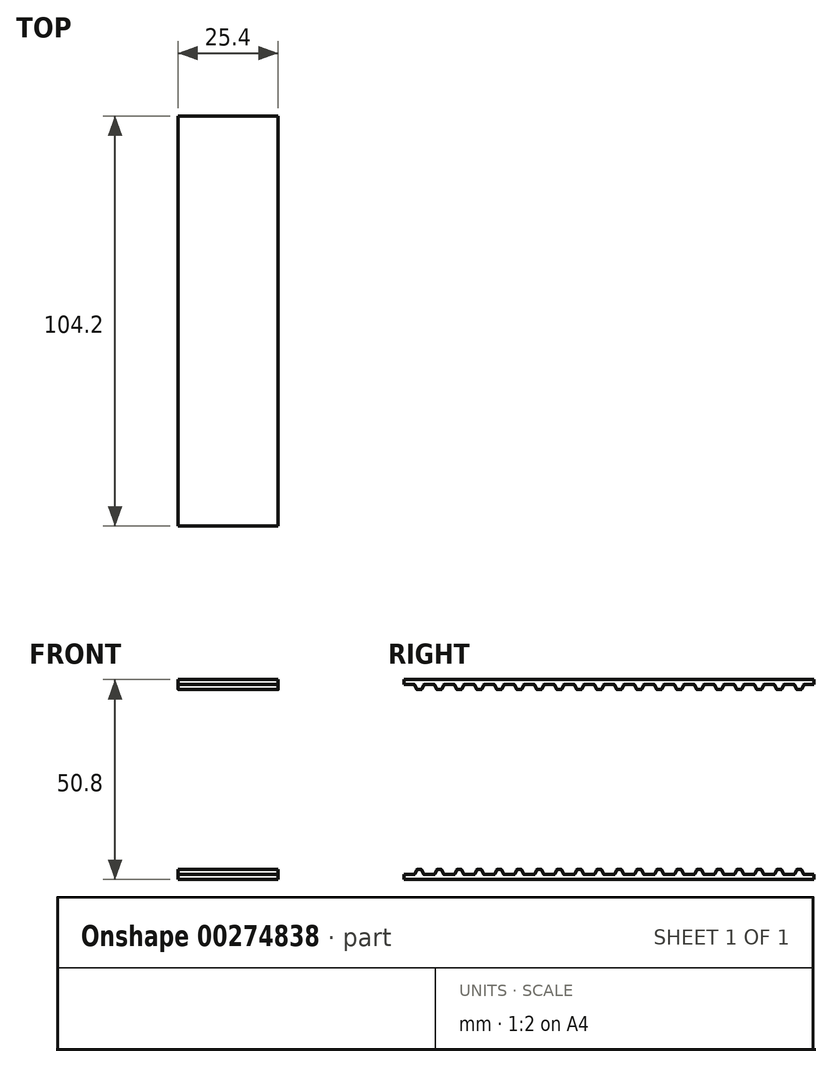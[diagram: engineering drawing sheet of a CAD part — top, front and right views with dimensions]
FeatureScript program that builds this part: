
annotation { "Feature Type Name" : "Feature", "Feature Type Description" : "" }
export const myFeature = defineFeature(function(context is Context, id is Id, definition is map)
    precondition{}
    {
        {
            var Q0;
            Q0=qCreatedBy(makeId("Right.planeOp"),FACE);
            var sketch = newSketch(context, id + "F0", { "sketchPlane" : qUnion([Q0])});
            skLineSegment(sketch, "E0", {"start": v(-151.26, 0) * mm, "end": v(153.54, 0) * mm, "construction": true});
            skLineSegment(sketch, "E1", {"start": v(-25.4, 25.4) * mm, "end": v(78.8, 25.4) * mm});
            skLineSegment(sketch, "E2", {"start": v(-25.4, 24.13) * mm, "end": v(-22.86, 24.13) * mm});
            skLineSegment(sketch, "E3", {"start": v(-22.62, 23.96) * mm, "end": v(-22.28, 23.03) * mm});
            skLineSegment(sketch, "E4", {"start": v(-22.04, 22.86) * mm, "end": v(-21.08, 22.86) * mm});
            skLineSegment(sketch, "E5", {"start": v(-20.84, 23.03) * mm, "end": v(-20.5, 23.96) * mm});
            skPoint(sketch, "E6", {"position": v(-22.45, 23.5) * mm});
            skPoint(sketch, "E7", {"position": v(-20.67, 23.5) * mm});
            skLineSegment(sketch, "E8", {"start": v(-20.26, 24.13) * mm, "end": v(-17.78, 24.13) * mm});
            skPoint(sketch, "E9.visualSharp", {"position": v(-22.68, 24.13) * mm});
            skArc(sketch, "E9.filletArc", {"start": v(-22.62, 23.96) * mm, "mid": v(-22.71, 24.08) * mm, "end": v(-22.86, 24.13) * mm});
            skPoint(sketch, "E10.visualSharp", {"position": v(-22.22, 22.86) * mm});
            skArc(sketch, "E10.filletArc", {"start": v(-22.28, 23.03) * mm, "mid": v(-22.19, 22.9) * mm, "end": v(-22.04, 22.86) * mm});
            skPoint(sketch, "E11.visualSharp", {"position": v(-20.9, 22.86) * mm});
            skArc(sketch, "E11.filletArc", {"start": v(-21.08, 22.86) * mm, "mid": v(-20.94, 22.9) * mm, "end": v(-20.84, 23.03) * mm});
            skPoint(sketch, "E12.visualSharp", {"position": v(-20.44, 24.13) * mm});
            skArc(sketch, "E12.filletArc", {"start": v(-20.26, 24.13) * mm, "mid": v(-20.4, 24.08) * mm, "end": v(-20.5, 23.96) * mm});
            skPoint(sketch, "E13.1.0.0", {"position": v(-15.82, 22.86) * mm});
            skLineSegment(sketch, "E13.1.0.1", {"start": v(-15.76, 23.03) * mm, "end": v(-15.42, 23.96) * mm});
            skLineSegment(sketch, "E13.1.0.2", {"start": v(-16.96, 22.86) * mm, "end": v(-16, 22.86) * mm});
            skLineSegment(sketch, "E13.1.0.3", {"start": v(-17.54, 23.96) * mm, "end": v(-17.2, 23.03) * mm});
            skPoint(sketch, "E13.1.0.4", {"position": v(-17.14, 22.86) * mm});
            skPoint(sketch, "E13.1.0.5", {"position": v(-15.36, 24.13) * mm});
            skPoint(sketch, "E13.1.0.6", {"position": v(-17.37, 23.5) * mm});
            skPoint(sketch, "E13.1.0.7", {"position": v(-17.6, 24.13) * mm});
            skPoint(sketch, "E13.1.0.8", {"position": v(-15.6, 23.5) * mm});
            skArc(sketch, "E13.1.0.9", {"start": v(-17.54, 23.96) * mm, "mid": v(-17.63, 24.08) * mm, "end": v(-17.78, 24.13) * mm});
            skArc(sketch, "E13.1.0.10", {"start": v(-17.2, 23.03) * mm, "mid": v(-17.1, 22.9) * mm, "end": v(-16.96, 22.86) * mm});
            skArc(sketch, "E13.1.0.11", {"start": v(-16, 22.86) * mm, "mid": v(-15.86, 22.9) * mm, "end": v(-15.76, 23.03) * mm});
            skArc(sketch, "E13.1.0.12", {"start": v(-15.18, 24.13) * mm, "mid": v(-15.33, 24.08) * mm, "end": v(-15.42, 23.96) * mm});
            skPoint(sketch, "E13.2.0.0", {"position": v(-10.74, 22.86) * mm});
            skLineSegment(sketch, "E13.2.0.1", {"start": v(-10.68, 23.03) * mm, "end": v(-10.34, 23.96) * mm});
            skLineSegment(sketch, "E13.2.0.2", {"start": v(-11.88, 22.86) * mm, "end": v(-10.92, 22.86) * mm});
            skLineSegment(sketch, "E13.2.0.3", {"start": v(-12.46, 23.96) * mm, "end": v(-12.12, 23.03) * mm});
            skPoint(sketch, "E13.2.0.4", {"position": v(-12.06, 22.86) * mm});
            skPoint(sketch, "E13.2.0.5", {"position": v(-10.28, 24.13) * mm});
            skPoint(sketch, "E13.2.0.6", {"position": v(-12.3, 23.5) * mm});
            skPoint(sketch, "E13.2.0.7", {"position": v(-12.52, 24.13) * mm});
            skPoint(sketch, "E13.2.0.8", {"position": v(-10.51, 23.5) * mm});
            skArc(sketch, "E13.2.0.9", {"start": v(-12.46, 23.96) * mm, "mid": v(-12.55, 24.08) * mm, "end": v(-12.7, 24.13) * mm});
            skArc(sketch, "E13.2.0.10", {"start": v(-12.12, 23.03) * mm, "mid": v(-12.03, 22.9) * mm, "end": v(-11.88, 22.86) * mm});
            skArc(sketch, "E13.2.0.11", {"start": v(-10.92, 22.86) * mm, "mid": v(-10.78, 22.9) * mm, "end": v(-10.68, 23.03) * mm});
            skArc(sketch, "E13.2.0.12", {"start": v(-10.1, 24.13) * mm, "mid": v(-10.25, 24.08) * mm, "end": v(-10.34, 23.96) * mm});
            skPoint(sketch, "E13.3.0.0", {"position": v(-5.66, 22.86) * mm});
            skLineSegment(sketch, "E13.3.0.1", {"start": v(-5.6, 23.03) * mm, "end": v(-5.26, 23.96) * mm});
            skLineSegment(sketch, "E13.3.0.2", {"start": v(-6.8, 22.86) * mm, "end": v(-5.84, 22.86) * mm});
            skLineSegment(sketch, "E13.3.0.3", {"start": v(-7.38, 23.96) * mm, "end": v(-7.04, 23.03) * mm});
            skPoint(sketch, "E13.3.0.4", {"position": v(-6.98, 22.86) * mm});
            skPoint(sketch, "E13.3.0.5", {"position": v(-5.2, 24.13) * mm});
            skPoint(sketch, "E13.3.0.6", {"position": v(-7.21, 23.5) * mm});
            skPoint(sketch, "E13.3.0.7", {"position": v(-7.44, 24.13) * mm});
            skPoint(sketch, "E13.3.0.8", {"position": v(-5.43, 23.5) * mm});
            skArc(sketch, "E13.3.0.9", {"start": v(-7.38, 23.96) * mm, "mid": v(-7.47, 24.08) * mm, "end": v(-7.62, 24.13) * mm});
            skArc(sketch, "E13.3.0.10", {"start": v(-7.04, 23.03) * mm, "mid": v(-6.95, 22.9) * mm, "end": v(-6.8, 22.86) * mm});
            skArc(sketch, "E13.3.0.11", {"start": v(-5.84, 22.86) * mm, "mid": v(-5.7, 22.9) * mm, "end": v(-5.6, 23.03) * mm});
            skArc(sketch, "E13.3.0.12", {"start": v(-5.02, 24.13) * mm, "mid": v(-5.17, 24.08) * mm, "end": v(-5.26, 23.96) * mm});
            skPoint(sketch, "E13.4.0.0", {"position": v(-0.58, 22.86) * mm});
            skLineSegment(sketch, "E13.4.0.1", {"start": v(-0.52, 23.03) * mm, "end": v(-0.18, 23.96) * mm});
            skLineSegment(sketch, "E13.4.0.2", {"start": v(-1.72, 22.86) * mm, "end": v(-0.76, 22.86) * mm});
            skLineSegment(sketch, "E13.4.0.3", {"start": v(-2.3, 23.96) * mm, "end": v(-1.96, 23.03) * mm});
            skPoint(sketch, "E13.4.0.4", {"position": v(-1.9, 22.86) * mm});
            skPoint(sketch, "E13.4.0.5", {"position": v(-0.12, 24.13) * mm});
            skPoint(sketch, "E13.4.0.6", {"position": v(-2.13, 23.5) * mm});
            skPoint(sketch, "E13.4.0.7", {"position": v(-2.36, 24.13) * mm});
            skPoint(sketch, "E13.4.0.8", {"position": v(-0.35, 23.5) * mm});
            skArc(sketch, "E13.4.0.9", {"start": v(-2.3, 23.96) * mm, "mid": v(-2.4, 24.08) * mm, "end": v(-2.54, 24.13) * mm});
            skArc(sketch, "E13.4.0.10", {"start": v(-1.96, 23.03) * mm, "mid": v(-1.87, 22.9) * mm, "end": v(-1.72, 22.86) * mm});
            skArc(sketch, "E13.4.0.11", {"start": v(-0.76, 22.86) * mm, "mid": v(-0.62, 22.9) * mm, "end": v(-0.52, 23.03) * mm});
            skArc(sketch, "E13.4.0.12", {"start": v(0.06, 24.13) * mm, "mid": v(-0.09, 24.08) * mm, "end": v(-0.18, 23.96) * mm});
            skPoint(sketch, "E13.5.0.0", {"position": v(4.5, 22.86) * mm});
            skLineSegment(sketch, "E13.5.0.1", {"start": v(4.56, 23.03) * mm, "end": v(4.9, 23.96) * mm});
            skLineSegment(sketch, "E13.5.0.2", {"start": v(3.36, 22.86) * mm, "end": v(4.32, 22.86) * mm});
            skLineSegment(sketch, "E13.5.0.3", {"start": v(2.78, 23.96) * mm, "end": v(3.12, 23.03) * mm});
            skPoint(sketch, "E13.5.0.4", {"position": v(3.18, 22.86) * mm});
            skPoint(sketch, "E13.5.0.5", {"position": v(4.96, 24.13) * mm});
            skPoint(sketch, "E13.5.0.6", {"position": v(2.95, 23.5) * mm});
            skPoint(sketch, "E13.5.0.7", {"position": v(2.72, 24.13) * mm});
            skPoint(sketch, "E13.5.0.8", {"position": v(4.73, 23.5) * mm});
            skArc(sketch, "E13.5.0.9", {"start": v(2.78, 23.96) * mm, "mid": v(2.69, 24.08) * mm, "end": v(2.54, 24.13) * mm});
            skArc(sketch, "E13.5.0.10", {"start": v(3.12, 23.03) * mm, "mid": v(3.21, 22.9) * mm, "end": v(3.36, 22.86) * mm});
            skArc(sketch, "E13.5.0.11", {"start": v(4.32, 22.86) * mm, "mid": v(4.46, 22.9) * mm, "end": v(4.56, 23.03) * mm});
            skArc(sketch, "E13.5.0.12", {"start": v(5.14, 24.13) * mm, "mid": v(5, 24.08) * mm, "end": v(4.9, 23.96) * mm});
            skPoint(sketch, "E13.6.0.0", {"position": v(9.58, 22.86) * mm});
            skLineSegment(sketch, "E13.6.0.1", {"start": v(9.64, 23.03) * mm, "end": v(9.98, 23.96) * mm});
            skLineSegment(sketch, "E13.6.0.2", {"start": v(8.44, 22.86) * mm, "end": v(9.4, 22.86) * mm});
            skLineSegment(sketch, "E13.6.0.3", {"start": v(7.86, 23.96) * mm, "end": v(8.2, 23.03) * mm});
            skPoint(sketch, "E13.6.0.4", {"position": v(8.26, 22.86) * mm});
            skPoint(sketch, "E13.6.0.5", {"position": v(10.04, 24.13) * mm});
            skPoint(sketch, "E13.6.0.6", {"position": v(8.03, 23.5) * mm});
            skPoint(sketch, "E13.6.0.7", {"position": v(7.8, 24.13) * mm});
            skPoint(sketch, "E13.6.0.8", {"position": v(9.8, 23.5) * mm});
            skArc(sketch, "E13.6.0.9", {"start": v(7.86, 23.96) * mm, "mid": v(7.77, 24.08) * mm, "end": v(7.62, 24.13) * mm});
            skArc(sketch, "E13.6.0.10", {"start": v(8.2, 23.03) * mm, "mid": v(8.3, 22.9) * mm, "end": v(8.44, 22.86) * mm});
            skArc(sketch, "E13.6.0.11", {"start": v(9.4, 22.86) * mm, "mid": v(9.54, 22.9) * mm, "end": v(9.64, 23.03) * mm});
            skArc(sketch, "E13.6.0.12", {"start": v(10.22, 24.13) * mm, "mid": v(10.07, 24.08) * mm, "end": v(9.98, 23.96) * mm});
            skPoint(sketch, "E13.7.0.0", {"position": v(14.66, 22.86) * mm});
            skLineSegment(sketch, "E13.7.0.1", {"start": v(14.72, 23.03) * mm, "end": v(15.06, 23.96) * mm});
            skLineSegment(sketch, "E13.7.0.2", {"start": v(13.52, 22.86) * mm, "end": v(14.48, 22.86) * mm});
            skLineSegment(sketch, "E13.7.0.3", {"start": v(12.94, 23.96) * mm, "end": v(13.28, 23.03) * mm});
            skPoint(sketch, "E13.7.0.4", {"position": v(13.34, 22.86) * mm});
            skPoint(sketch, "E13.7.0.5", {"position": v(15.12, 24.13) * mm});
            skPoint(sketch, "E13.7.0.6", {"position": v(13.1, 23.5) * mm});
            skPoint(sketch, "E13.7.0.7", {"position": v(12.88, 24.13) * mm});
            skPoint(sketch, "E13.7.0.8", {"position": v(14.89, 23.5) * mm});
            skArc(sketch, "E13.7.0.9", {"start": v(12.94, 23.96) * mm, "mid": v(12.85, 24.08) * mm, "end": v(12.7, 24.13) * mm});
            skArc(sketch, "E13.7.0.10", {"start": v(13.28, 23.03) * mm, "mid": v(13.37, 22.9) * mm, "end": v(13.52, 22.86) * mm});
            skArc(sketch, "E13.7.0.11", {"start": v(14.48, 22.86) * mm, "mid": v(14.62, 22.9) * mm, "end": v(14.72, 23.03) * mm});
            skArc(sketch, "E13.7.0.12", {"start": v(15.3, 24.13) * mm, "mid": v(15.15, 24.08) * mm, "end": v(15.06, 23.96) * mm});
            skPoint(sketch, "E13.8.0.0", {"position": v(19.74, 22.86) * mm});
            skLineSegment(sketch, "E13.8.0.1", {"start": v(19.8, 23.03) * mm, "end": v(20.14, 23.96) * mm});
            skLineSegment(sketch, "E13.8.0.2", {"start": v(18.6, 22.86) * mm, "end": v(19.56, 22.86) * mm});
            skLineSegment(sketch, "E13.8.0.3", {"start": v(18.02, 23.96) * mm, "end": v(18.36, 23.03) * mm});
            skPoint(sketch, "E13.8.0.4", {"position": v(18.42, 22.86) * mm});
            skPoint(sketch, "E13.8.0.5", {"position": v(20.2, 24.13) * mm});
            skPoint(sketch, "E13.8.0.6", {"position": v(18.19, 23.5) * mm});
            skPoint(sketch, "E13.8.0.7", {"position": v(17.96, 24.13) * mm});
            skPoint(sketch, "E13.8.0.8", {"position": v(19.97, 23.5) * mm});
            skArc(sketch, "E13.8.0.9", {"start": v(18.02, 23.96) * mm, "mid": v(17.93, 24.08) * mm, "end": v(17.78, 24.13) * mm});
            skArc(sketch, "E13.8.0.10", {"start": v(18.36, 23.03) * mm, "mid": v(18.45, 22.9) * mm, "end": v(18.6, 22.86) * mm});
            skArc(sketch, "E13.8.0.11", {"start": v(19.56, 22.86) * mm, "mid": v(19.7, 22.9) * mm, "end": v(19.8, 23.03) * mm});
            skArc(sketch, "E13.8.0.12", {"start": v(20.38, 24.13) * mm, "mid": v(20.23, 24.08) * mm, "end": v(20.14, 23.96) * mm});
            skPoint(sketch, "E13.9.0.0", {"position": v(24.82, 22.86) * mm});
            skLineSegment(sketch, "E13.9.0.1", {"start": v(24.88, 23.03) * mm, "end": v(25.22, 23.96) * mm});
            skLineSegment(sketch, "E13.9.0.2", {"start": v(23.68, 22.86) * mm, "end": v(24.64, 22.86) * mm});
            skLineSegment(sketch, "E13.9.0.3", {"start": v(23.1, 23.96) * mm, "end": v(23.44, 23.03) * mm});
            skPoint(sketch, "E13.9.0.4", {"position": v(23.5, 22.86) * mm});
            skPoint(sketch, "E13.9.0.5", {"position": v(25.28, 24.13) * mm});
            skPoint(sketch, "E13.9.0.6", {"position": v(23.27, 23.5) * mm});
            skPoint(sketch, "E13.9.0.7", {"position": v(23.04, 24.13) * mm});
            skPoint(sketch, "E13.9.0.8", {"position": v(25.05, 23.5) * mm});
            skArc(sketch, "E13.9.0.9", {"start": v(23.1, 23.96) * mm, "mid": v(23, 24.08) * mm, "end": v(22.86, 24.13) * mm});
            skArc(sketch, "E13.9.0.10", {"start": v(23.44, 23.03) * mm, "mid": v(23.53, 22.9) * mm, "end": v(23.68, 22.86) * mm});
            skArc(sketch, "E13.9.0.11", {"start": v(24.64, 22.86) * mm, "mid": v(24.78, 22.9) * mm, "end": v(24.88, 23.03) * mm});
            skArc(sketch, "E13.9.0.12", {"start": v(25.46, 24.13) * mm, "mid": v(25.31, 24.08) * mm, "end": v(25.22, 23.96) * mm});
            skPoint(sketch, "E13.10.0.0", {"position": v(29.9, 22.86) * mm});
            skLineSegment(sketch, "E13.10.0.1", {"start": v(29.96, 23.03) * mm, "end": v(30.3, 23.96) * mm});
            skLineSegment(sketch, "E13.10.0.2", {"start": v(28.76, 22.86) * mm, "end": v(29.72, 22.86) * mm});
            skLineSegment(sketch, "E13.10.0.3", {"start": v(28.18, 23.96) * mm, "end": v(28.52, 23.03) * mm});
            skPoint(sketch, "E13.10.0.4", {"position": v(28.58, 22.86) * mm});
            skPoint(sketch, "E13.10.0.5", {"position": v(30.36, 24.13) * mm});
            skPoint(sketch, "E13.10.0.6", {"position": v(28.35, 23.5) * mm});
            skPoint(sketch, "E13.10.0.7", {"position": v(28.12, 24.13) * mm});
            skPoint(sketch, "E13.10.0.8", {"position": v(30.13, 23.5) * mm});
            skArc(sketch, "E13.10.0.9", {"start": v(28.18, 23.96) * mm, "mid": v(28.09, 24.08) * mm, "end": v(27.94, 24.13) * mm});
            skArc(sketch, "E13.10.0.10", {"start": v(28.52, 23.03) * mm, "mid": v(28.61, 22.9) * mm, "end": v(28.76, 22.86) * mm});
            skArc(sketch, "E13.10.0.11", {"start": v(29.72, 22.86) * mm, "mid": v(29.86, 22.9) * mm, "end": v(29.96, 23.03) * mm});
            skArc(sketch, "E13.10.0.12", {"start": v(30.54, 24.13) * mm, "mid": v(30.4, 24.08) * mm, "end": v(30.3, 23.96) * mm});
            skPoint(sketch, "E13.11.0.0", {"position": v(34.98, 22.86) * mm});
            skLineSegment(sketch, "E13.11.0.1", {"start": v(35.04, 23.03) * mm, "end": v(35.38, 23.96) * mm});
            skLineSegment(sketch, "E13.11.0.2", {"start": v(33.84, 22.86) * mm, "end": v(34.8, 22.86) * mm});
            skLineSegment(sketch, "E13.11.0.3", {"start": v(33.26, 23.96) * mm, "end": v(33.6, 23.03) * mm});
            skPoint(sketch, "E13.11.0.4", {"position": v(33.66, 22.86) * mm});
            skPoint(sketch, "E13.11.0.5", {"position": v(35.44, 24.13) * mm});
            skPoint(sketch, "E13.11.0.6", {"position": v(33.43, 23.5) * mm});
            skPoint(sketch, "E13.11.0.7", {"position": v(33.2, 24.13) * mm});
            skPoint(sketch, "E13.11.0.8", {"position": v(35.2, 23.5) * mm});
            skArc(sketch, "E13.11.0.9", {"start": v(33.26, 23.96) * mm, "mid": v(33.17, 24.08) * mm, "end": v(33.02, 24.13) * mm});
            skArc(sketch, "E13.11.0.10", {"start": v(33.6, 23.03) * mm, "mid": v(33.7, 22.9) * mm, "end": v(33.84, 22.86) * mm});
            skArc(sketch, "E13.11.0.11", {"start": v(34.8, 22.86) * mm, "mid": v(34.94, 22.9) * mm, "end": v(35.04, 23.03) * mm});
            skArc(sketch, "E13.11.0.12", {"start": v(35.62, 24.13) * mm, "mid": v(35.47, 24.08) * mm, "end": v(35.38, 23.96) * mm});
            skPoint(sketch, "E13.12.0.0", {"position": v(40.06, 22.86) * mm});
            skLineSegment(sketch, "E13.12.0.1", {"start": v(40.12, 23.03) * mm, "end": v(40.46, 23.96) * mm});
            skLineSegment(sketch, "E13.12.0.2", {"start": v(38.92, 22.86) * mm, "end": v(39.88, 22.86) * mm});
            skLineSegment(sketch, "E13.12.0.3", {"start": v(38.34, 23.96) * mm, "end": v(38.68, 23.03) * mm});
            skPoint(sketch, "E13.12.0.4", {"position": v(38.74, 22.86) * mm});
            skPoint(sketch, "E13.12.0.5", {"position": v(40.52, 24.13) * mm});
            skPoint(sketch, "E13.12.0.6", {"position": v(38.5, 23.5) * mm});
            skPoint(sketch, "E13.12.0.7", {"position": v(38.28, 24.13) * mm});
            skPoint(sketch, "E13.12.0.8", {"position": v(40.29, 23.5) * mm});
            skArc(sketch, "E13.12.0.9", {"start": v(38.34, 23.96) * mm, "mid": v(38.25, 24.08) * mm, "end": v(38.1, 24.13) * mm});
            skArc(sketch, "E13.12.0.10", {"start": v(38.68, 23.03) * mm, "mid": v(38.77, 22.9) * mm, "end": v(38.92, 22.86) * mm});
            skArc(sketch, "E13.12.0.11", {"start": v(39.88, 22.86) * mm, "mid": v(40.02, 22.9) * mm, "end": v(40.12, 23.03) * mm});
            skArc(sketch, "E13.12.0.12", {"start": v(40.7, 24.13) * mm, "mid": v(40.55, 24.08) * mm, "end": v(40.46, 23.96) * mm});
            skPoint(sketch, "E13.13.0.0", {"position": v(45.14, 22.86) * mm});
            skLineSegment(sketch, "E13.13.0.1", {"start": v(45.2, 23.03) * mm, "end": v(45.54, 23.96) * mm});
            skLineSegment(sketch, "E13.13.0.2", {"start": v(44, 22.86) * mm, "end": v(44.96, 22.86) * mm});
            skLineSegment(sketch, "E13.13.0.3", {"start": v(43.42, 23.96) * mm, "end": v(43.76, 23.03) * mm});
            skPoint(sketch, "E13.13.0.4", {"position": v(43.82, 22.86) * mm});
            skPoint(sketch, "E13.13.0.5", {"position": v(45.6, 24.13) * mm});
            skPoint(sketch, "E13.13.0.6", {"position": v(43.59, 23.5) * mm});
            skPoint(sketch, "E13.13.0.7", {"position": v(43.36, 24.13) * mm});
            skPoint(sketch, "E13.13.0.8", {"position": v(45.37, 23.5) * mm});
            skArc(sketch, "E13.13.0.9", {"start": v(43.42, 23.96) * mm, "mid": v(43.33, 24.08) * mm, "end": v(43.18, 24.13) * mm});
            skArc(sketch, "E13.13.0.10", {"start": v(43.76, 23.03) * mm, "mid": v(43.85, 22.9) * mm, "end": v(44, 22.86) * mm});
            skArc(sketch, "E13.13.0.11", {"start": v(44.96, 22.86) * mm, "mid": v(45.1, 22.9) * mm, "end": v(45.2, 23.03) * mm});
            skArc(sketch, "E13.13.0.12", {"start": v(45.78, 24.13) * mm, "mid": v(45.63, 24.08) * mm, "end": v(45.54, 23.96) * mm});
            skPoint(sketch, "E13.14.0.0", {"position": v(50.22, 22.86) * mm});
            skLineSegment(sketch, "E13.14.0.1", {"start": v(50.28, 23.03) * mm, "end": v(50.62, 23.96) * mm});
            skLineSegment(sketch, "E13.14.0.2", {"start": v(49.08, 22.86) * mm, "end": v(50.04, 22.86) * mm});
            skLineSegment(sketch, "E13.14.0.3", {"start": v(48.5, 23.96) * mm, "end": v(48.84, 23.03) * mm});
            skPoint(sketch, "E13.14.0.4", {"position": v(48.9, 22.86) * mm});
            skPoint(sketch, "E13.14.0.5", {"position": v(50.68, 24.13) * mm});
            skPoint(sketch, "E13.14.0.6", {"position": v(48.67, 23.5) * mm});
            skPoint(sketch, "E13.14.0.7", {"position": v(48.44, 24.13) * mm});
            skPoint(sketch, "E13.14.0.8", {"position": v(50.45, 23.5) * mm});
            skArc(sketch, "E13.14.0.9", {"start": v(48.5, 23.96) * mm, "mid": v(48.4, 24.08) * mm, "end": v(48.26, 24.13) * mm});
            skArc(sketch, "E13.14.0.10", {"start": v(48.84, 23.03) * mm, "mid": v(48.93, 22.9) * mm, "end": v(49.08, 22.86) * mm});
            skArc(sketch, "E13.14.0.11", {"start": v(50.04, 22.86) * mm, "mid": v(50.18, 22.9) * mm, "end": v(50.28, 23.03) * mm});
            skArc(sketch, "E13.14.0.12", {"start": v(50.86, 24.13) * mm, "mid": v(50.71, 24.08) * mm, "end": v(50.62, 23.96) * mm});
            skPoint(sketch, "E13.15.0.0", {"position": v(55.3, 22.86) * mm});
            skLineSegment(sketch, "E13.15.0.1", {"start": v(55.36, 23.03) * mm, "end": v(55.7, 23.96) * mm});
            skLineSegment(sketch, "E13.15.0.2", {"start": v(54.16, 22.86) * mm, "end": v(55.12, 22.86) * mm});
            skLineSegment(sketch, "E13.15.0.3", {"start": v(53.58, 23.96) * mm, "end": v(53.92, 23.03) * mm});
            skPoint(sketch, "E13.15.0.4", {"position": v(53.98, 22.86) * mm});
            skPoint(sketch, "E13.15.0.5", {"position": v(55.76, 24.13) * mm});
            skPoint(sketch, "E13.15.0.6", {"position": v(53.75, 23.5) * mm});
            skPoint(sketch, "E13.15.0.7", {"position": v(53.52, 24.13) * mm});
            skPoint(sketch, "E13.15.0.8", {"position": v(55.53, 23.5) * mm});
            skArc(sketch, "E13.15.0.9", {"start": v(53.58, 23.96) * mm, "mid": v(53.49, 24.08) * mm, "end": v(53.34, 24.13) * mm});
            skArc(sketch, "E13.15.0.10", {"start": v(53.92, 23.03) * mm, "mid": v(54.01, 22.9) * mm, "end": v(54.16, 22.86) * mm});
            skArc(sketch, "E13.15.0.11", {"start": v(55.12, 22.86) * mm, "mid": v(55.26, 22.9) * mm, "end": v(55.36, 23.03) * mm});
            skArc(sketch, "E13.15.0.12", {"start": v(55.94, 24.13) * mm, "mid": v(55.8, 24.08) * mm, "end": v(55.7, 23.96) * mm});
            skPoint(sketch, "E13.16.0.0", {"position": v(60.38, 22.86) * mm});
            skLineSegment(sketch, "E13.16.0.1", {"start": v(60.44, 23.03) * mm, "end": v(60.78, 23.96) * mm});
            skLineSegment(sketch, "E13.16.0.2", {"start": v(59.24, 22.86) * mm, "end": v(60.2, 22.86) * mm});
            skLineSegment(sketch, "E13.16.0.3", {"start": v(58.66, 23.96) * mm, "end": v(59, 23.03) * mm});
            skPoint(sketch, "E13.16.0.4", {"position": v(59.06, 22.86) * mm});
            skPoint(sketch, "E13.16.0.5", {"position": v(60.84, 24.13) * mm});
            skPoint(sketch, "E13.16.0.6", {"position": v(58.83, 23.5) * mm});
            skPoint(sketch, "E13.16.0.7", {"position": v(58.6, 24.13) * mm});
            skPoint(sketch, "E13.16.0.8", {"position": v(60.6, 23.5) * mm});
            skArc(sketch, "E13.16.0.9", {"start": v(58.66, 23.96) * mm, "mid": v(58.57, 24.08) * mm, "end": v(58.42, 24.13) * mm});
            skArc(sketch, "E13.16.0.10", {"start": v(59, 23.03) * mm, "mid": v(59.1, 22.9) * mm, "end": v(59.24, 22.86) * mm});
            skArc(sketch, "E13.16.0.11", {"start": v(60.2, 22.86) * mm, "mid": v(60.34, 22.9) * mm, "end": v(60.44, 23.03) * mm});
            skArc(sketch, "E13.16.0.12", {"start": v(61.02, 24.13) * mm, "mid": v(60.87, 24.08) * mm, "end": v(60.78, 23.96) * mm});
            skPoint(sketch, "E13.17.0.0", {"position": v(65.46, 22.86) * mm});
            skLineSegment(sketch, "E13.17.0.1", {"start": v(65.52, 23.03) * mm, "end": v(65.86, 23.96) * mm});
            skLineSegment(sketch, "E13.17.0.2", {"start": v(64.32, 22.86) * mm, "end": v(65.28, 22.86) * mm});
            skLineSegment(sketch, "E13.17.0.3", {"start": v(63.74, 23.96) * mm, "end": v(64.08, 23.03) * mm});
            skPoint(sketch, "E13.17.0.4", {"position": v(64.14, 22.86) * mm});
            skPoint(sketch, "E13.17.0.5", {"position": v(65.92, 24.13) * mm});
            skPoint(sketch, "E13.17.0.6", {"position": v(63.9, 23.5) * mm});
            skPoint(sketch, "E13.17.0.7", {"position": v(63.68, 24.13) * mm});
            skPoint(sketch, "E13.17.0.8", {"position": v(65.69, 23.5) * mm});
            skArc(sketch, "E13.17.0.9", {"start": v(63.74, 23.96) * mm, "mid": v(63.65, 24.08) * mm, "end": v(63.5, 24.13) * mm});
            skArc(sketch, "E13.17.0.10", {"start": v(64.08, 23.03) * mm, "mid": v(64.17, 22.9) * mm, "end": v(64.32, 22.86) * mm});
            skArc(sketch, "E13.17.0.11", {"start": v(65.28, 22.86) * mm, "mid": v(65.42, 22.9) * mm, "end": v(65.52, 23.03) * mm});
            skArc(sketch, "E13.17.0.12", {"start": v(66.1, 24.13) * mm, "mid": v(65.95, 24.08) * mm, "end": v(65.86, 23.96) * mm});
            skPoint(sketch, "E13.18.0.0", {"position": v(70.54, 22.86) * mm});
            skLineSegment(sketch, "E13.18.0.1", {"start": v(70.6, 23.03) * mm, "end": v(70.94, 23.96) * mm});
            skLineSegment(sketch, "E13.18.0.2", {"start": v(69.4, 22.86) * mm, "end": v(70.36, 22.86) * mm});
            skLineSegment(sketch, "E13.18.0.3", {"start": v(68.82, 23.96) * mm, "end": v(69.16, 23.03) * mm});
            skPoint(sketch, "E13.18.0.4", {"position": v(69.22, 22.86) * mm});
            skPoint(sketch, "E13.18.0.5", {"position": v(71, 24.13) * mm});
            skPoint(sketch, "E13.18.0.6", {"position": v(68.99, 23.5) * mm});
            skPoint(sketch, "E13.18.0.7", {"position": v(68.76, 24.13) * mm});
            skPoint(sketch, "E13.18.0.8", {"position": v(70.77, 23.5) * mm});
            skArc(sketch, "E13.18.0.9", {"start": v(68.82, 23.96) * mm, "mid": v(68.73, 24.08) * mm, "end": v(68.58, 24.13) * mm});
            skArc(sketch, "E13.18.0.10", {"start": v(69.16, 23.03) * mm, "mid": v(69.25, 22.9) * mm, "end": v(69.4, 22.86) * mm});
            skArc(sketch, "E13.18.0.11", {"start": v(70.36, 22.86) * mm, "mid": v(70.5, 22.9) * mm, "end": v(70.6, 23.03) * mm});
            skArc(sketch, "E13.18.0.12", {"start": v(71.18, 24.13) * mm, "mid": v(71.03, 24.08) * mm, "end": v(70.94, 23.96) * mm});
            skPoint(sketch, "E13.19.0.0", {"position": v(75.62, 22.86) * mm});
            skLineSegment(sketch, "E13.19.0.1", {"start": v(75.68, 23.03) * mm, "end": v(76.02, 23.96) * mm});
            skLineSegment(sketch, "E13.19.0.2", {"start": v(74.48, 22.86) * mm, "end": v(75.44, 22.86) * mm});
            skLineSegment(sketch, "E13.19.0.3", {"start": v(73.9, 23.96) * mm, "end": v(74.24, 23.03) * mm});
            skPoint(sketch, "E13.19.0.4", {"position": v(74.3, 22.86) * mm});
            skPoint(sketch, "E13.19.0.5", {"position": v(76.08, 24.13) * mm});
            skPoint(sketch, "E13.19.0.6", {"position": v(74.07, 23.5) * mm});
            skPoint(sketch, "E13.19.0.7", {"position": v(73.84, 24.13) * mm});
            skPoint(sketch, "E13.19.0.8", {"position": v(75.85, 23.5) * mm});
            skArc(sketch, "E13.19.0.9", {"start": v(73.9, 23.96) * mm, "mid": v(73.8, 24.08) * mm, "end": v(73.66, 24.13) * mm});
            skArc(sketch, "E13.19.0.10", {"start": v(74.24, 23.03) * mm, "mid": v(74.33, 22.9) * mm, "end": v(74.48, 22.86) * mm});
            skArc(sketch, "E13.19.0.11", {"start": v(75.44, 22.86) * mm, "mid": v(75.58, 22.9) * mm, "end": v(75.68, 23.03) * mm});
            skArc(sketch, "E13.19.0.12", {"start": v(76.26, 24.13) * mm, "mid": v(76.11, 24.08) * mm, "end": v(76.02, 23.96) * mm});
            skLineSegment(sketch, "E13.direction1", {"start": v(-22.22, 22.86) * mm, "end": v(-17.14, 22.86) * mm, "construction": true});
            skLineSegment(sketch, "E14.trimOffspring", {"start": v(-15.18, 24.13) * mm, "end": v(-12.7, 24.13) * mm});
            skLineSegment(sketch, "E15", {"start": v(-10.1, 24.13) * mm, "end": v(-7.62, 24.13) * mm});
            skLineSegment(sketch, "E16", {"start": v(-5.02, 24.13) * mm, "end": v(-2.54, 24.13) * mm});
            skLineSegment(sketch, "E17", {"start": v(0.06, 24.13) * mm, "end": v(2.54, 24.13) * mm});
            skLineSegment(sketch, "E18", {"start": v(5.14, 24.13) * mm, "end": v(7.62, 24.13) * mm});
            skLineSegment(sketch, "E19", {"start": v(10.22, 24.13) * mm, "end": v(12.7, 24.13) * mm});
            skLineSegment(sketch, "E20", {"start": v(15.3, 24.13) * mm, "end": v(17.78, 24.13) * mm});
            skLineSegment(sketch, "E21", {"start": v(20.38, 24.13) * mm, "end": v(22.86, 24.13) * mm});
            skLineSegment(sketch, "E22", {"start": v(25.46, 24.13) * mm, "end": v(27.94, 24.13) * mm});
            skLineSegment(sketch, "E23", {"start": v(30.54, 24.13) * mm, "end": v(33.02, 24.13) * mm});
            skLineSegment(sketch, "E24", {"start": v(35.62, 24.13) * mm, "end": v(38.1, 24.13) * mm});
            skLineSegment(sketch, "E25", {"start": v(40.7, 24.13) * mm, "end": v(43.18, 24.13) * mm});
            skLineSegment(sketch, "E26", {"start": v(45.78, 24.13) * mm, "end": v(48.26, 24.13) * mm});
            skLineSegment(sketch, "E27", {"start": v(50.86, 24.13) * mm, "end": v(53.34, 24.13) * mm});
            skLineSegment(sketch, "E28", {"start": v(55.94, 24.13) * mm, "end": v(58.42, 24.13) * mm});
            skLineSegment(sketch, "E29", {"start": v(61.02, 24.13) * mm, "end": v(63.5, 24.13) * mm});
            skLineSegment(sketch, "E30", {"start": v(66.1, 24.13) * mm, "end": v(68.58, 24.13) * mm});
            skLineSegment(sketch, "E31", {"start": v(71.18, 24.13) * mm, "end": v(73.66, 24.13) * mm});
            skLineSegment(sketch, "E32", {"start": v(76.26, 24.13) * mm, "end": v(78.8, 24.13) * mm});
            skLineSegment(sketch, "E33", {"start": v(78.8, 24.13) * mm, "end": v(78.8, 25.4) * mm});
            skLineSegment(sketch, "E34", {"start": v(-25.4, 25.4) * mm, "end": v(-25.4, 24.13) * mm});
            skPoint(sketch, "E35.orphan", {"position": v(-25.4, 23.11) * mm});
            skSolve(sketch);
        }
        {
            var Q0;
            Q0 = qSketchRegion(id + "F0", true);
            extrude(context, id + "F1", {"entities" : qUnion([Q0]), "depth" : 12.7 * mm, "hasSecondDirection" : true, "secondDirectionOppositeDirection" : true, "secondDirectionDepth" : 12.7 * mm});
        }
        {
            var Q0;
            Q0=makeQuery(id+"F1.opExtrude","SWEPT_BODY",BODY,{"disambiguationData":[OSD([sQuery(id+"F0.wireOp",EDGE,"E1"),sQuery(id+"F0.wireOp",EDGE,"E2"),sQuery(id+"F0.wireOp",EDGE,"E3"),sQuery(id+"F0.wireOp",EDGE,"E4"),sQuery(id+"F0.wireOp",EDGE,"E5"),sQuery(id+"F0.wireOp",EDGE,"E8"),sQuery(id+"F0.wireOp",EDGE,"E9.filletArc"),sQuery(id+"F0.wireOp",EDGE,"E10.filletArc"),sQuery(id+"F0.wireOp",EDGE,"E11.filletArc"),sQuery(id+"F0.wireOp",EDGE,"E12.filletArc"),sQuery(id+"F0.wireOp",EDGE,"E13.1.0.1"),sQuery(id+"F0.wireOp",EDGE,"E13.1.0.2"),sQuery(id+"F0.wireOp",EDGE,"E13.1.0.3"),sQuery(id+"F0.wireOp",EDGE,"E13.1.0.9"),sQuery(id+"F0.wireOp",EDGE,"E13.1.0.10"),sQuery(id+"F0.wireOp",EDGE,"E13.1.0.11"),sQuery(id+"F0.wireOp",EDGE,"E13.1.0.12"),sQuery(id+"F0.wireOp",EDGE,"E13.2.0.1"),sQuery(id+"F0.wireOp",EDGE,"E13.2.0.2"),sQuery(id+"F0.wireOp",EDGE,"E13.2.0.3"),sQuery(id+"F0.wireOp",EDGE,"E13.2.0.9"),sQuery(id+"F0.wireOp",EDGE,"E13.2.0.10"),sQuery(id+"F0.wireOp",EDGE,"E13.2.0.11"),sQuery(id+"F0.wireOp",EDGE,"E13.2.0.12"),sQuery(id+"F0.wireOp",EDGE,"E13.3.0.1"),sQuery(id+"F0.wireOp",EDGE,"E13.3.0.2"),sQuery(id+"F0.wireOp",EDGE,"E13.3.0.3"),sQuery(id+"F0.wireOp",EDGE,"E13.3.0.9"),sQuery(id+"F0.wireOp",EDGE,"E13.3.0.10"),sQuery(id+"F0.wireOp",EDGE,"E13.3.0.11"),sQuery(id+"F0.wireOp",EDGE,"E13.3.0.12"),sQuery(id+"F0.wireOp",EDGE,"E13.4.0.1"),sQuery(id+"F0.wireOp",EDGE,"E13.4.0.2"),sQuery(id+"F0.wireOp",EDGE,"E13.4.0.3"),sQuery(id+"F0.wireOp",EDGE,"E13.4.0.9"),sQuery(id+"F0.wireOp",EDGE,"E13.4.0.10"),sQuery(id+"F0.wireOp",EDGE,"E13.4.0.11"),sQuery(id+"F0.wireOp",EDGE,"E13.4.0.12"),sQuery(id+"F0.wireOp",EDGE,"E13.5.0.1"),sQuery(id+"F0.wireOp",EDGE,"E13.5.0.2"),sQuery(id+"F0.wireOp",EDGE,"E13.5.0.3"),sQuery(id+"F0.wireOp",EDGE,"E13.5.0.9"),sQuery(id+"F0.wireOp",EDGE,"E13.5.0.10"),sQuery(id+"F0.wireOp",EDGE,"E13.5.0.11"),sQuery(id+"F0.wireOp",EDGE,"E13.5.0.12"),sQuery(id+"F0.wireOp",EDGE,"E13.6.0.1"),sQuery(id+"F0.wireOp",EDGE,"E13.6.0.2"),sQuery(id+"F0.wireOp",EDGE,"E13.6.0.3"),sQuery(id+"F0.wireOp",EDGE,"E13.6.0.9"),sQuery(id+"F0.wireOp",EDGE,"E13.6.0.10"),sQuery(id+"F0.wireOp",EDGE,"E13.6.0.11"),sQuery(id+"F0.wireOp",EDGE,"E13.6.0.12"),sQuery(id+"F0.wireOp",EDGE,"E13.7.0.1"),sQuery(id+"F0.wireOp",EDGE,"E13.7.0.2"),sQuery(id+"F0.wireOp",EDGE,"E13.7.0.3"),sQuery(id+"F0.wireOp",EDGE,"E13.7.0.9"),sQuery(id+"F0.wireOp",EDGE,"E13.7.0.10"),sQuery(id+"F0.wireOp",EDGE,"E13.7.0.11"),sQuery(id+"F0.wireOp",EDGE,"E13.7.0.12"),sQuery(id+"F0.wireOp",EDGE,"E13.8.0.1"),sQuery(id+"F0.wireOp",EDGE,"E13.8.0.2"),sQuery(id+"F0.wireOp",EDGE,"E13.8.0.3"),sQuery(id+"F0.wireOp",EDGE,"E13.8.0.9"),sQuery(id+"F0.wireOp",EDGE,"E13.8.0.10"),sQuery(id+"F0.wireOp",EDGE,"E13.8.0.11"),sQuery(id+"F0.wireOp",EDGE,"E13.8.0.12"),sQuery(id+"F0.wireOp",EDGE,"E13.9.0.1"),sQuery(id+"F0.wireOp",EDGE,"E13.9.0.2"),sQuery(id+"F0.wireOp",EDGE,"E13.9.0.3"),sQuery(id+"F0.wireOp",EDGE,"E13.9.0.9"),sQuery(id+"F0.wireOp",EDGE,"E13.9.0.10"),sQuery(id+"F0.wireOp",EDGE,"E13.9.0.11"),sQuery(id+"F0.wireOp",EDGE,"E13.9.0.12"),sQuery(id+"F0.wireOp",EDGE,"E13.10.0.1"),sQuery(id+"F0.wireOp",EDGE,"E13.10.0.2"),sQuery(id+"F0.wireOp",EDGE,"E13.10.0.3"),sQuery(id+"F0.wireOp",EDGE,"E13.10.0.9"),sQuery(id+"F0.wireOp",EDGE,"E13.10.0.10"),sQuery(id+"F0.wireOp",EDGE,"E13.10.0.11"),sQuery(id+"F0.wireOp",EDGE,"E13.10.0.12"),sQuery(id+"F0.wireOp",EDGE,"E13.11.0.1"),sQuery(id+"F0.wireOp",EDGE,"E13.11.0.2"),sQuery(id+"F0.wireOp",EDGE,"E13.11.0.3"),sQuery(id+"F0.wireOp",EDGE,"E13.11.0.9"),sQuery(id+"F0.wireOp",EDGE,"E13.11.0.10"),sQuery(id+"F0.wireOp",EDGE,"E13.11.0.11"),sQuery(id+"F0.wireOp",EDGE,"E13.11.0.12"),sQuery(id+"F0.wireOp",EDGE,"E13.12.0.1"),sQuery(id+"F0.wireOp",EDGE,"E13.12.0.2"),sQuery(id+"F0.wireOp",EDGE,"E13.12.0.3"),sQuery(id+"F0.wireOp",EDGE,"E13.12.0.9"),sQuery(id+"F0.wireOp",EDGE,"E13.12.0.10"),sQuery(id+"F0.wireOp",EDGE,"E13.12.0.11"),sQuery(id+"F0.wireOp",EDGE,"E13.12.0.12"),sQuery(id+"F0.wireOp",EDGE,"E13.13.0.1"),sQuery(id+"F0.wireOp",EDGE,"E13.13.0.2"),sQuery(id+"F0.wireOp",EDGE,"E13.13.0.3"),sQuery(id+"F0.wireOp",EDGE,"E13.13.0.9"),sQuery(id+"F0.wireOp",EDGE,"E13.13.0.10"),sQuery(id+"F0.wireOp",EDGE,"E13.13.0.11"),sQuery(id+"F0.wireOp",EDGE,"E13.13.0.12"),sQuery(id+"F0.wireOp",EDGE,"E13.14.0.1"),sQuery(id+"F0.wireOp",EDGE,"E13.14.0.2"),sQuery(id+"F0.wireOp",EDGE,"E13.14.0.3"),sQuery(id+"F0.wireOp",EDGE,"E13.14.0.9"),sQuery(id+"F0.wireOp",EDGE,"E13.14.0.10"),sQuery(id+"F0.wireOp",EDGE,"E13.14.0.11"),sQuery(id+"F0.wireOp",EDGE,"E13.14.0.12"),sQuery(id+"F0.wireOp",EDGE,"E13.15.0.1"),sQuery(id+"F0.wireOp",EDGE,"E13.15.0.2"),sQuery(id+"F0.wireOp",EDGE,"E13.15.0.3"),sQuery(id+"F0.wireOp",EDGE,"E13.15.0.9"),sQuery(id+"F0.wireOp",EDGE,"E13.15.0.10"),sQuery(id+"F0.wireOp",EDGE,"E13.15.0.11"),sQuery(id+"F0.wireOp",EDGE,"E13.15.0.12"),sQuery(id+"F0.wireOp",EDGE,"E13.16.0.1"),sQuery(id+"F0.wireOp",EDGE,"E13.16.0.2"),sQuery(id+"F0.wireOp",EDGE,"E13.16.0.3"),sQuery(id+"F0.wireOp",EDGE,"E13.16.0.9"),sQuery(id+"F0.wireOp",EDGE,"E13.16.0.10"),sQuery(id+"F0.wireOp",EDGE,"E13.16.0.11"),sQuery(id+"F0.wireOp",EDGE,"E13.16.0.12"),sQuery(id+"F0.wireOp",EDGE,"E13.17.0.1"),sQuery(id+"F0.wireOp",EDGE,"E13.17.0.2"),sQuery(id+"F0.wireOp",EDGE,"E13.17.0.3"),sQuery(id+"F0.wireOp",EDGE,"E13.17.0.9"),sQuery(id+"F0.wireOp",EDGE,"E13.17.0.10"),sQuery(id+"F0.wireOp",EDGE,"E13.17.0.11"),sQuery(id+"F0.wireOp",EDGE,"E13.17.0.12"),sQuery(id+"F0.wireOp",EDGE,"E13.18.0.1"),sQuery(id+"F0.wireOp",EDGE,"E13.18.0.2"),sQuery(id+"F0.wireOp",EDGE,"E13.18.0.3"),sQuery(id+"F0.wireOp",EDGE,"E13.18.0.9"),sQuery(id+"F0.wireOp",EDGE,"E13.18.0.10"),sQuery(id+"F0.wireOp",EDGE,"E13.18.0.11"),sQuery(id+"F0.wireOp",EDGE,"E13.18.0.12"),sQuery(id+"F0.wireOp",EDGE,"E13.19.0.1"),sQuery(id+"F0.wireOp",EDGE,"E13.19.0.2"),sQuery(id+"F0.wireOp",EDGE,"E13.19.0.3"),sQuery(id+"F0.wireOp",EDGE,"E13.19.0.9"),sQuery(id+"F0.wireOp",EDGE,"E13.19.0.10"),sQuery(id+"F0.wireOp",EDGE,"E13.19.0.11"),sQuery(id+"F0.wireOp",EDGE,"E13.19.0.12"),sQuery(id+"F0.wireOp",EDGE,"E14.trimOffspring"),sQuery(id+"F0.wireOp",EDGE,"E15"),sQuery(id+"F0.wireOp",EDGE,"E16"),sQuery(id+"F0.wireOp",EDGE,"E17"),sQuery(id+"F0.wireOp",EDGE,"E18"),sQuery(id+"F0.wireOp",EDGE,"E19"),sQuery(id+"F0.wireOp",EDGE,"E20"),sQuery(id+"F0.wireOp",EDGE,"E21"),sQuery(id+"F0.wireOp",EDGE,"E22"),sQuery(id+"F0.wireOp",EDGE,"E23"),sQuery(id+"F0.wireOp",EDGE,"E24"),sQuery(id+"F0.wireOp",EDGE,"E25"),sQuery(id+"F0.wireOp",EDGE,"E26"),sQuery(id+"F0.wireOp",EDGE,"E27"),sQuery(id+"F0.wireOp",EDGE,"E28"),sQuery(id+"F0.wireOp",EDGE,"E29"),sQuery(id+"F0.wireOp",EDGE,"E30"),sQuery(id+"F0.wireOp",EDGE,"E31"),sQuery(id+"F0.wireOp",EDGE,"E32"),sQuery(id+"F0.wireOp",EDGE,"E33"),sQuery(id+"F0.wireOp",EDGE,"E34")])]});
            var Q1;
            Q1=qCreatedBy(makeId("Top.planeOp"),FACE);
            mirror(context, id + "F2", {"entities" : qUnion([Q0]), "mirrorPlane" : qUnion([Q1])});
        }
    });
